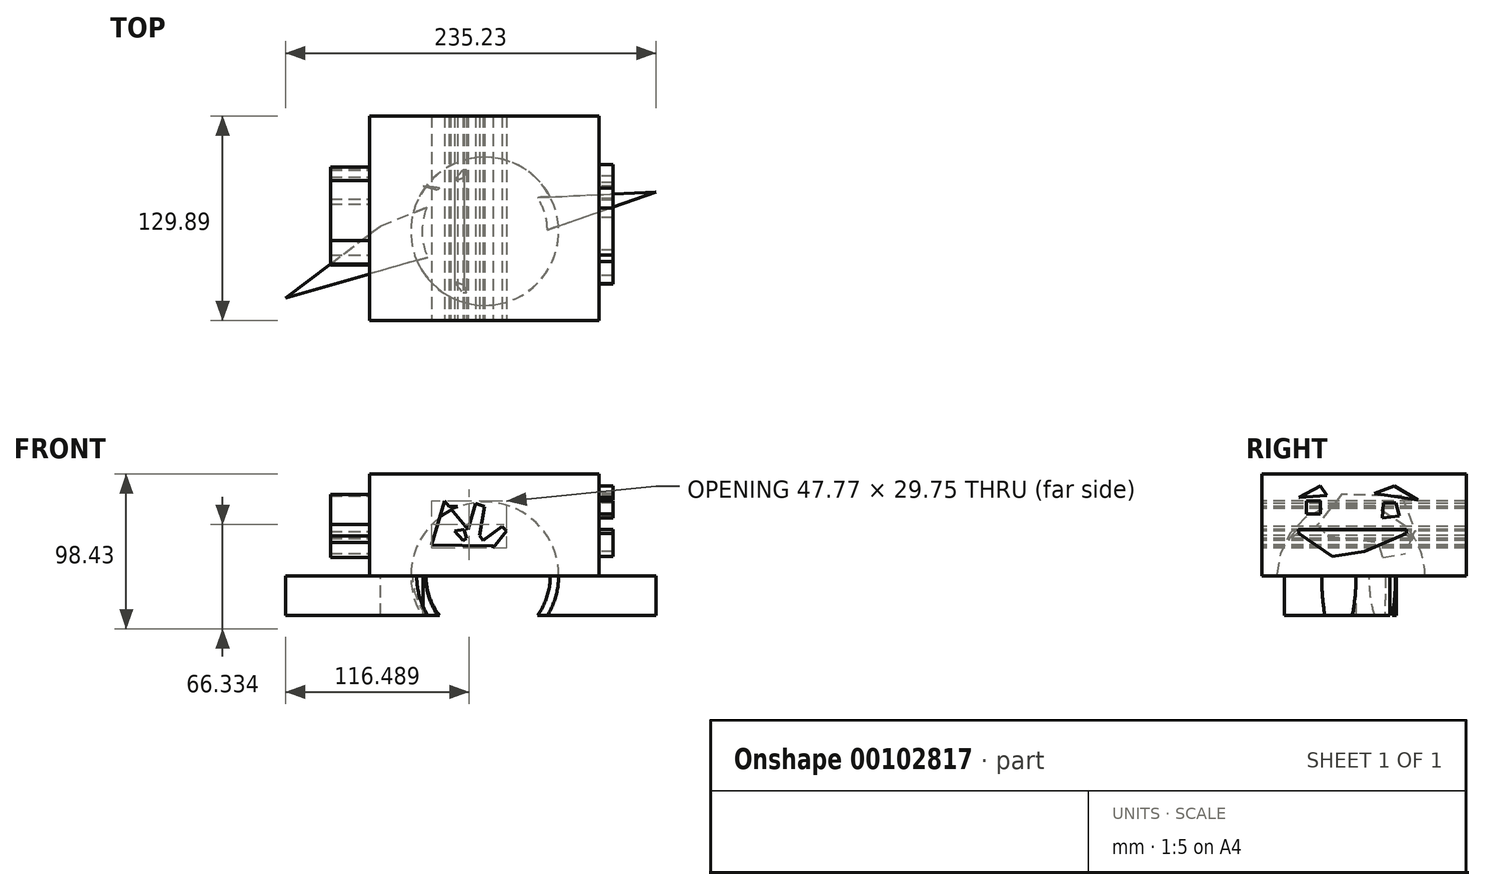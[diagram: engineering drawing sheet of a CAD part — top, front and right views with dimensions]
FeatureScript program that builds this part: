
annotation { "Feature Type Name" : "Feature", "Feature Type Description" : "" }
export const myFeature = defineFeature(function(context is Context, id is Id, definition is map)
    precondition{}
    {
        {
            var Q0;
            Q0=qCreatedBy(makeId("Top.planeOp"),FACE);
            var sketch = newSketch(context, id + "F0", { "sketchPlane" : qUnion([Q0])});
            skLineSegment(sketch, "E0.bottom", {"start": v(72.53, 73.26) * mm, "end": v(-72.96, 73.26) * mm});
            skLineSegment(sketch, "E0.top", {"start": v(72.53, -56.63) * mm, "end": v(-72.96, -56.63) * mm});
            skLineSegment(sketch, "E0.left", {"start": v(72.53, 73.26) * mm, "end": v(72.53, -56.63) * mm});
            skLineSegment(sketch, "E0.right", {"start": v(-72.96, 73.26) * mm, "end": v(-72.96, -56.63) * mm});
            skSolve(sketch);
        }
        {
            var Q0;
            Q0=makeQuery(id+"F0.imprint","IMPRINT",FACE,{"disambiguationData":[TD([[makeQuery(id+"F0.imprint","IMPRINT",EDGE,{"derivedFrom":sQuery(id+"F0.wireOp",EDGE,"E0.bottom")}),1.0]])]});
            extrude(context, id + "F1", {"entities" : qUnion([Q0]), "depth" : 64.8 * mm, "offsetDistance" : 25 * mm});
        }
        {
            var Q0;
            Q0=qCreatedBy(makeId("Top.planeOp"),FACE);
            var sketch = newSketch(context, id + "F2", { "sketchPlane" : qUnion([Q0])});
            skCircle(sketch, "E1", {"center": v(0, 0) * mm, "radius": 47.05 * mm});
            skLineSegment(sketch, "E2", {"start": v(6.95, -46.53) * mm, "end": v(-6.87, 46.54) * mm});
            skSolve(sketch);
        }
        {
            var Q0;
            {var subQ0=sQuery(id+"F2.wireOp",EDGE,"E2");Q0=makeQuery(id+"F2.imprint","IMPRINT",FACE,{"disambiguationData":[TD([[makeQuery(id+"F2.imprint","IMPRINT",EDGE,{"derivedFrom":subQ0}),-1.0]])]});}
            var Q1;
            Q1=sQuery(id+"F2.wireOp",EDGE,"E2");
            revolve(context, id + "F3", {"entities" : qUnion([Q0]), "axis" : qUnion([Q1]), "revolveType" : RevolveType.FULL});
        }
        {
            var Q0;
            Q0=makeQuery(id+"F1.opExtrude","SWEPT_FACE",FACE,{"disambiguationData":[OSD([sQuery(id+"F0.wireOp",EDGE,"E0.left")])]});
            var sketch = newSketch(context, id + "F4", { "sketchPlane" : qUnion([Q0])});
            skLineSegment(sketch, "E3", {"start": v(-28.12, 47.51) * mm, "end": v(-19.32, 47.51) * mm});
            skLineSegment(sketch, "E4", {"start": v(-19.32, 47.51) * mm, "end": v(-19.32, 39.35) * mm});
            skLineSegment(sketch, "E5", {"start": v(-28.12, 47.51) * mm, "end": v(-28.12, 39.41) * mm});
            skLineSegment(sketch, "E6", {"start": v(-28.12, 39.41) * mm, "end": v(-19.32, 39.35) * mm});
            skLineSegment(sketch, "E7", {"start": v(20.78, 46.43) * mm, "end": v(19.89, 36.74) * mm});
            skLineSegment(sketch, "E8", {"start": v(19.89, 36.74) * mm, "end": v(30.92, 38.14) * mm});
            skLineSegment(sketch, "E9", {"start": v(30.92, 38.14) * mm, "end": v(28.69, 46.43) * mm});
            skLineSegment(sketch, "E10", {"start": v(20.78, 46.43) * mm, "end": v(28.69, 46.43) * mm});
            skLineSegment(sketch, "E11", {"start": v(-33.03, 27.04) * mm, "end": v(-11.86, 12.57) * mm});
            skLineSegment(sketch, "E12", {"start": v(-11.86, 12.57) * mm, "end": v(8.6, 15.7) * mm});
            skLineSegment(sketch, "E13", {"start": v(8.6, 15.7) * mm, "end": v(35.13, 26.92) * mm});
            skLineSegment(sketch, "E14", {"start": v(35.13, 26.92) * mm, "end": v(35.13, 29.53) * mm});
            skLineSegment(sketch, "E15", {"start": v(-33.03, 27.04) * mm, "end": v(-33.35, 29.53) * mm});
            skLineSegment(sketch, "E16", {"start": v(14.85, 52.48) * mm, "end": v(27.54, 57.08) * mm});
            skLineSegment(sketch, "E17", {"start": v(27.54, 57.08) * mm, "end": v(42.52, 48.34) * mm});
            skLineSegment(sketch, "E18", {"start": v(35.13, 29.53) * mm, "end": v(-3.32, 29.53) * mm});
            skLineSegment(sketch, "E19", {"start": v(-3.32, 29.53) * mm, "end": v(-33.35, 29.53) * mm});
            skLineSegment(sketch, "E20", {"start": v(-33.03, 49.74) * mm, "end": v(-19.32, 57.08) * mm});
            skLineSegment(sketch, "E21", {"start": v(-19.32, 57.08) * mm, "end": v(-15.12, 51.02) * mm});
            skLineSegment(sketch, "E22", {"start": v(-15.12, 51.02) * mm, "end": v(-33.03, 49.74) * mm});
            skLineSegment(sketch, "E23", {"start": v(14.85, 52.48) * mm, "end": v(42.52, 48.34) * mm});
            skSolve(sketch);
        }
        {
            var Q0;
            Q0 = qSketchRegion(id + "F4", true);
            extrude(context, id + "F5", {"entities" : qUnion([Q0]), "operationType" : NewBodyOperationType.ADD, "depth" : 9.1 * mm, "offsetDistance" : 25 * mm});
        }
        {
            var Q0;
            Q0=makeQuery(id+"F1.opExtrude","SWEPT_FACE",FACE,{"disambiguationData":[OSD([sQuery(id+"F0.wireOp",EDGE,"E0.top")])]});
            var sketch = newSketch(context, id + "F6", { "sketchPlane" : qUnion([Q0])});
            skLineSegment(sketch, "E24", {"start": v(-0.94, 22.46) * mm, "end": v(11.05, 31.41) * mm});
            skLineSegment(sketch, "E25", {"start": v(11.05, 31.41) * mm, "end": v(13.93, 28.6) * mm});
            skLineSegment(sketch, "E26", {"start": v(13.93, 28.6) * mm, "end": v(5.43, 17.83) * mm});
            skLineSegment(sketch, "E27", {"start": v(-0.94, 22.46) * mm, "end": v(-3.37, 25.7) * mm});
            skLineSegment(sketch, "E28", {"start": v(-3.37, 25.7) * mm, "end": v(0, 44.16) * mm});
            skLineSegment(sketch, "E29", {"start": v(0, 44.16) * mm, "end": v(-5.72, 46.06) * mm});
            skLineSegment(sketch, "E30", {"start": v(-5.72, 46.06) * mm, "end": v(-10.58, 29.67) * mm});
            skLineSegment(sketch, "E31", {"start": v(-10.58, 29.67) * mm, "end": v(-25.53, 47.58) * mm});
            skLineSegment(sketch, "E32", {"start": v(17.73, 52.8) * mm, "end": v(-21.72, 43.02) * mm});
            skLineSegment(sketch, "E33", {"start": v(-21.72, 43.02) * mm, "end": v(-21.34, 42.56) * mm});
            skLineSegment(sketch, "E34", {"start": v(-21.34, 42.56) * mm, "end": v(-21.72, 43.02) * mm});
            skLineSegment(sketch, "E35", {"start": v(-22.68, 44.16) * mm, "end": v(-17.12, 44.16) * mm});
            skLineSegment(sketch, "E36", {"start": v(-34.33, 19.65) * mm, "end": v(67.96, 17.83) * mm});
            skLineSegment(sketch, "E37", {"start": v(-34.1, 18.74) * mm, "end": v(-25.53, 47.58) * mm});
            skLineSegment(sketch, "E38", {"start": v(5.43, 18.94) * mm, "end": v(5.43, 17.83) * mm});
            skLineSegment(sketch, "E39", {"start": v(5.43, 18.94) * mm, "end": v(67.96, 17.83) * mm});
            skLineSegment(sketch, "E40", {"start": v(68.95, 17.83) * mm, "end": v(67.96, 17.83) * mm});
            skLineSegment(sketch, "E41", {"start": v(67.96, 17.83) * mm, "end": v(69.87, 17.8) * mm});
            skLineSegment(sketch, "E42", {"start": v(-11.56, 23.75) * mm, "end": v(-13.03, 29.67) * mm});
            skLineSegment(sketch, "E43", {"start": v(-13.03, 29.67) * mm, "end": v(-19, 28.6) * mm});
            skLineSegment(sketch, "E44", {"start": v(-19, 28.6) * mm, "end": v(-13.87, 22.46) * mm});
            skLineSegment(sketch, "E45", {"start": v(-13.87, 22.46) * mm, "end": v(-11.56, 23.75) * mm});
            skSolve(sketch);
        }
        {
            var Q0;
            Q0 = qSketchRegion(id + "F6", true);
            extrude(context, id + "F7", {"entities" : qUnion([Q0]), "operationType" : NewBodyOperationType.REMOVE, "oppositeDirection" : true, "depth" : 194.8 * mm, "offsetDistance" : 25 * mm});
        }
        {
            var Q0;
            Q0=makeQuery(id+"F1.opExtrude","SWEPT_FACE",FACE,{"disambiguationData":[OSD([sQuery(id+"F0.wireOp",EDGE,"E0.right")])]});
            var sketch = newSketch(context, id + "F8", { "sketchPlane" : qUnion([Q0])});
            skLineSegment(sketch, "E46", {"start": v(-32.7, 50.76) * mm, "end": v(5.87, 51.78) * mm});
            skLineSegment(sketch, "E47", {"start": v(5.87, 51.78) * mm, "end": v(-4.78, 51.5) * mm});
            skLineSegment(sketch, "E48", {"start": v(5.87, 51.78) * mm, "end": v(20.8, 32.78) * mm});
            skLineSegment(sketch, "E49", {"start": v(-32.26, 50.77) * mm, "end": v(-40.87, 28.38) * mm});
            skLineSegment(sketch, "E50", {"start": v(-40.36, 28.38) * mm, "end": v(-34.62, 14.16) * mm});
            skLineSegment(sketch, "E51", {"start": v(21.5, 32.78) * mm, "end": v(0, 8.87) * mm});
            skLineSegment(sketch, "E52", {"start": v(0, 8.36) * mm, "end": v(-34.62, 14.16) * mm});
            skLineSegment(sketch, "E53", {"start": v(-20.4, 11.78) * mm, "end": v(-7.72, 51.42) * mm});
            skLineSegment(sketch, "E54", {"start": v(-7.72, 51.42) * mm, "end": v(14.92, 25.47) * mm});
            skLineSegment(sketch, "E55", {"start": v(14.92, 25.47) * mm, "end": v(-17.35, 21.33) * mm});
            skLineSegment(sketch, "E56", {"start": v(-17.35, 21.33) * mm, "end": v(-33.8, 46.78) * mm});
            skLineSegment(sketch, "E57", {"start": v(-33.8, 46.78) * mm, "end": v(-27.42, 50.9) * mm});
            skLineSegment(sketch, "E58", {"start": v(-27.42, 50.9) * mm, "end": v(-14.8, 51.24) * mm});
            skLineSegment(sketch, "E59", {"start": v(-14.8, 51.24) * mm, "end": v(-9.63, 45.45) * mm});
            skLineSegment(sketch, "E60", {"start": v(-9.63, 45.45) * mm, "end": v(-11.61, 39.25) * mm});
            skLineSegment(sketch, "E61", {"start": v(-11.61, 39.25) * mm, "end": v(-25.24, 34.63) * mm});
            skLineSegment(sketch, "E62", {"start": v(-25.24, 34.63) * mm, "end": v(-39.6, 23.8) * mm});
            skLineSegment(sketch, "E63", {"start": v(-40.36, 28.38) * mm, "end": v(-40.87, 28.38) * mm});
            skLineSegment(sketch, "E64", {"start": v(21.5, 32.78) * mm, "end": v(20.8, 32.78) * mm});
            skLineSegment(sketch, "E65", {"start": v(-39.6, 23.8) * mm, "end": v(-39.11, 25.3) * mm});
            skSolve(sketch);
        }
        {
            var Q0;
            Q0 = qSketchRegion(id + "F8", true);
            var Q1;
            {var subQ21=sQuery(id+"F8.wireOp",EDGE,"E47");Q1=makeQuery(id+"F8.imprint","IMPRINT",FACE,{"disambiguationData":[TD([[makeQuery(id+"F8.imprint","IMPRINT",EDGE,{"derivedFrom":subQ21}),-1.0]])]});}
            extrude(context, id + "F9", {"entities" : qUnion([Q0, Q1]), "operationType" : NewBodyOperationType.ADD, "depth" : 25 * mm, "offsetDistance" : 25 * mm});
        }
        {
            var Q0;
            {var subQ0=sQuery(id+"F0.wireOp",EDGE,"E0.right");Q0=makeQuery(id+"F9.boolean.opBoolean","MERGE",FACE,{"derivedFrom":[makeQuery(id+"F1.opExtrude","CAP_FACE",FACE,{"disambiguationData":[OSD([sQuery(id+"F0.wireOp",EDGE,"E0.bottom"),sQuery(id+"F0.wireOp",EDGE,"E0.top"),sQuery(id+"F0.wireOp",EDGE,"E0.left"),subQ0])],"isStart":true}),makeQuery(id+"F9.opExtrude","SWEPT_FACE",FACE,{"disambiguationData":[OSD([subQ0]),TDD([makeQuery(id+"F8.imprint","IMPRINT",EDGE,{"derivedFrom":makeQuery(id+"F1.opExtrude","CAP_EDGE",EDGE,{"disambiguationData":[OSD([subQ0])],"isStart":true})})])]})]});}
            var sketch = newSketch(context, id + "F10", { "sketchPlane" : qUnion([Q0])});
            skLineSegment(sketch, "E66", {"start": v(-46.31, 8.43) * mm, "end": v(6.56, 8.43) * mm});
            skLineSegment(sketch, "E67", {"start": v(6.56, 8.43) * mm, "end": v(11.48, 3.94) * mm});
            skLineSegment(sketch, "E68", {"start": v(11.48, 3.94) * mm, "end": v(9.02, 6.19) * mm});
            skLineSegment(sketch, "E69", {"start": v(9.02, 6.19) * mm, "end": v(11.48, 8.9) * mm});
            skLineSegment(sketch, "E70", {"start": v(12.36, 8.43) * mm, "end": v(11.48, 8.9) * mm});
            skLineSegment(sketch, "E71", {"start": v(13.12, 8.43) * mm, "end": v(12.36, 8.43) * mm});
            skLineSegment(sketch, "E72", {"start": v(10.25, 5.07) * mm, "end": v(12.36, 8.43) * mm});
            skLineSegment(sketch, "E73", {"start": v(13.12, 8.43) * mm, "end": v(108.8, -24.84) * mm});
            skLineSegment(sketch, "E74", {"start": v(108.8, -24.84) * mm, "end": v(-126.44, 42.25) * mm});
            skLineSegment(sketch, "E75", {"start": v(-126.44, 42.25) * mm, "end": v(-66.02, -3.5) * mm});
            skLineSegment(sketch, "E76", {"start": v(-66.02, -3.5) * mm, "end": v(-17.2, -22.98) * mm});
            skLineSegment(sketch, "E77", {"start": v(-17.2, -22.98) * mm, "end": v(-38.98, -28.79) * mm});
            skLineSegment(sketch, "E78", {"start": v(-38.98, -28.79) * mm, "end": v(24.07, -21.12) * mm});
            skLineSegment(sketch, "E79", {"start": v(24.07, -21.12) * mm, "end": v(108.8, -24.84) * mm});
            skLineSegment(sketch, "E80", {"start": v(-26.17, -1.75) * mm, "end": v(-46.31, 7.45) * mm});
            skLineSegment(sketch, "E81", {"start": v(-46.31, 8.43) * mm, "end": v(-66.02, -3.5) * mm});
            skSolve(sketch);
        }
        {
            var Q0;
            Q0 = qSketchRegion(id + "F10", true);
            extrude(context, id + "F11", {"entities" : qUnion([Q0]), "operationType" : NewBodyOperationType.ADD, "depth" : 25 * mm, "offsetDistance" : 25 * mm});
        }
    });
